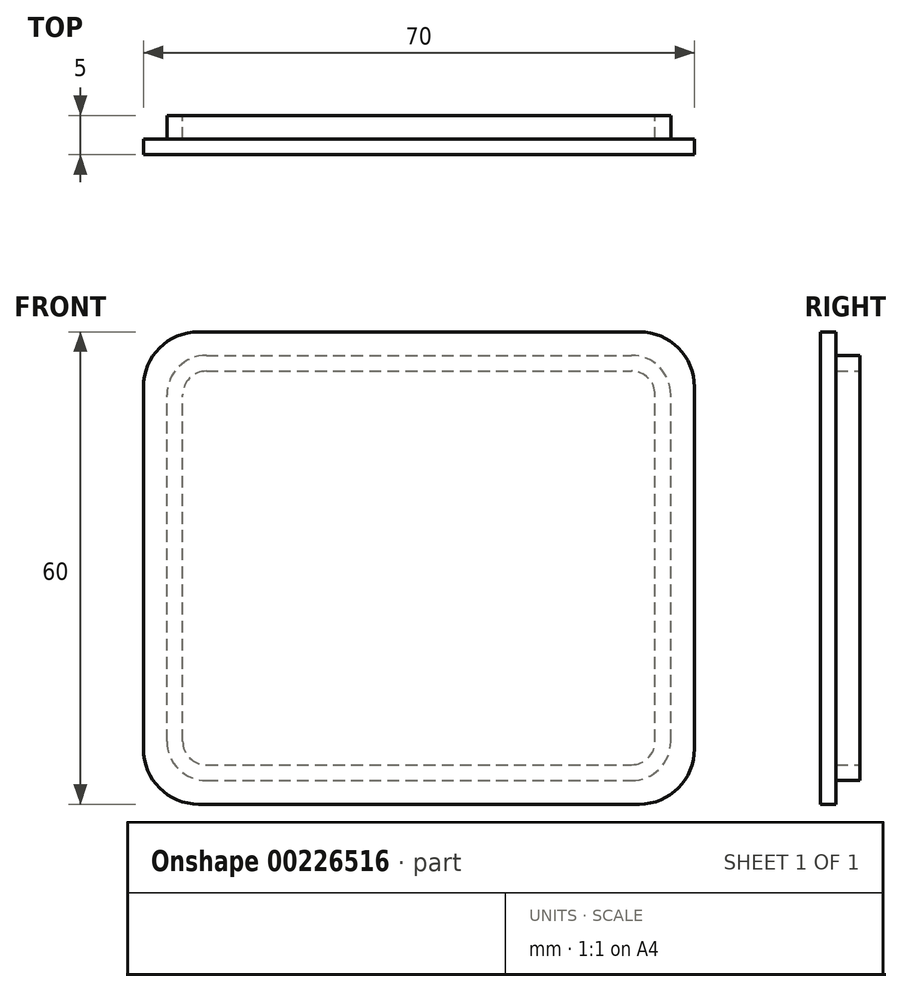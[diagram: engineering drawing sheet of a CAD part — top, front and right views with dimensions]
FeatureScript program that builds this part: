
annotation { "Feature Type Name" : "Feature", "Feature Type Description" : "" }
export const myFeature = defineFeature(function(context is Context, id is Id, definition is map)
    precondition{}
    {
        {
            var Q0;
            Q0=qCreatedBy(makeId("Front.planeOp"),FACE);
            var sketch = newSketch(context, id + "F0", { "sketchPlane" : qUnion([Q0])});
            skLineSegment(sketch, "E0.bottom", {"start": v(35, 30) * mm, "end": v(-35, 30) * mm});
            skLineSegment(sketch, "E0.top", {"start": v(35, -30) * mm, "end": v(-35, -30) * mm});
            skLineSegment(sketch, "E0.left", {"start": v(35, 30) * mm, "end": v(35, -30) * mm});
            skLineSegment(sketch, "E0.right", {"start": v(-35, 30) * mm, "end": v(-35, -30) * mm});
            skPoint(sketch, "E0.middle", {"position": v(0, 0) * mm});
            skSolve(sketch);
        }
        {
            var Q0;
            Q0=makeQuery(id+"F0.imprint","IMPRINT",FACE,{"disambiguationData":[TD([[makeQuery(id+"F0.imprint","IMPRINT",EDGE,{"derivedFrom":sQuery(id+"F0.wireOp",EDGE,"E0.bottom")}),1.0]])]});
            extrude(context, id + "F1", {"entities" : qUnion([Q0]), "depth" : 2 * mm});
        }
        {
            var Q0;
            Q0=makeQuery(id+"F1.opExtrude","SWEPT_EDGE",EDGE,{"disambiguationData":[OSD([sQuery(id+"F0.wireOp",EDGE,"E0.bottom"),sQuery(id+"F0.wireOp",EDGE,"E0.right")])]});
            var Q1;
            Q1=makeQuery(id+"F1.opExtrude","SWEPT_EDGE",EDGE,{"disambiguationData":[OSD([sQuery(id+"F0.wireOp",EDGE,"E0.bottom"),sQuery(id+"F0.wireOp",EDGE,"E0.left")])]});
            var Q2;
            Q2=makeQuery(id+"F1.opExtrude","SWEPT_EDGE",EDGE,{"disambiguationData":[OSD([sQuery(id+"F0.wireOp",EDGE,"E0.top"),sQuery(id+"F0.wireOp",EDGE,"E0.left")])]});
            var Q3;
            Q3=makeQuery(id+"F1.opExtrude","SWEPT_EDGE",EDGE,{"disambiguationData":[OSD([sQuery(id+"F0.wireOp",EDGE,"E0.top"),sQuery(id+"F0.wireOp",EDGE,"E0.right")])]});
            fillet(context, id + "F2", {"entities" : qUnion([Q0, Q1, Q2, Q3]), "radius" : 7 * mm, "tangentPropagation" : true, "allowEdgeOverflow" : false});
        }
        {
            var Q0;
            Q0=makeQuery(id+"F1.opExtrude","CAP_FACE",FACE,{"disambiguationData":[OSD([sQuery(id+"F0.wireOp",EDGE,"E0.bottom"),sQuery(id+"F0.wireOp",EDGE,"E0.top"),sQuery(id+"F0.wireOp",EDGE,"E0.left"),sQuery(id+"F0.wireOp",EDGE,"E0.right")])],"isStart":true});
            var sketch = newSketch(context, id + "F3", { "sketchPlane" : qUnion([Q0])});
            skLineSegment(sketch, "E1.bottom", {"start": v(32, -27) * mm, "end": v(-32, -27) * mm});
            skLineSegment(sketch, "E1.top", {"start": v(32, 27) * mm, "end": v(-32, 27) * mm});
            skLineSegment(sketch, "E1.left", {"start": v(32, -27) * mm, "end": v(32, 27) * mm});
            skLineSegment(sketch, "E1.right", {"start": v(-32, -27) * mm, "end": v(-32, 27) * mm});
            skPoint(sketch, "E1.middle", {"position": v(0, 0) * mm});
            skSolve(sketch);
        }
        {
            var Q0;
            Q0 = qSketchRegion(id + "F3", true);
            extrude(context, id + "F4", {"entities" : qUnion([Q0]), "operationType" : NewBodyOperationType.ADD, "depth" : 3 * mm});
        }
        {
            var Q0;
            Q0=makeQuery(id+"F4.opExtrude","SWEPT_EDGE",EDGE,{"disambiguationData":[OSD([sQuery(id+"F3.wireOp",EDGE,"E1.top"),sQuery(id+"F3.wireOp",EDGE,"E1.right")])]});
            var Q1;
            Q1=makeQuery(id+"F4.opExtrude","SWEPT_EDGE",EDGE,{"disambiguationData":[OSD([sQuery(id+"F3.wireOp",EDGE,"E1.top"),sQuery(id+"F3.wireOp",EDGE,"E1.left")])]});
            var Q2;
            Q2=makeQuery(id+"F4.opExtrude","SWEPT_EDGE",EDGE,{"disambiguationData":[OSD([sQuery(id+"F3.wireOp",EDGE,"E1.bottom"),sQuery(id+"F3.wireOp",EDGE,"E1.right")])]});
            var Q3;
            Q3=makeQuery(id+"F4.opExtrude","SWEPT_EDGE",EDGE,{"disambiguationData":[OSD([sQuery(id+"F3.wireOp",EDGE,"E1.bottom"),sQuery(id+"F3.wireOp",EDGE,"E1.left")])]});
            fillet(context, id + "F5", {"entities" : qUnion([Q0, Q1, Q2, Q3]), "radius" : 5 * mm, "tangentPropagation" : true, "allowEdgeOverflow" : false});
        }
        {
            var Q0;
            Q0=makeQuery(id+"F4.opExtrude","CAP_FACE",FACE,{"disambiguationData":[OSD([sQuery(id+"F3.wireOp",EDGE,"E1.bottom"),sQuery(id+"F3.wireOp",EDGE,"E1.top"),sQuery(id+"F3.wireOp",EDGE,"E1.left"),sQuery(id+"F3.wireOp",EDGE,"E1.right")])],"isStart":false});
            shell(context, id + "F6", {"entities" : qUnion([Q0]), "thickness" : 2 * mm});
        }
    });
